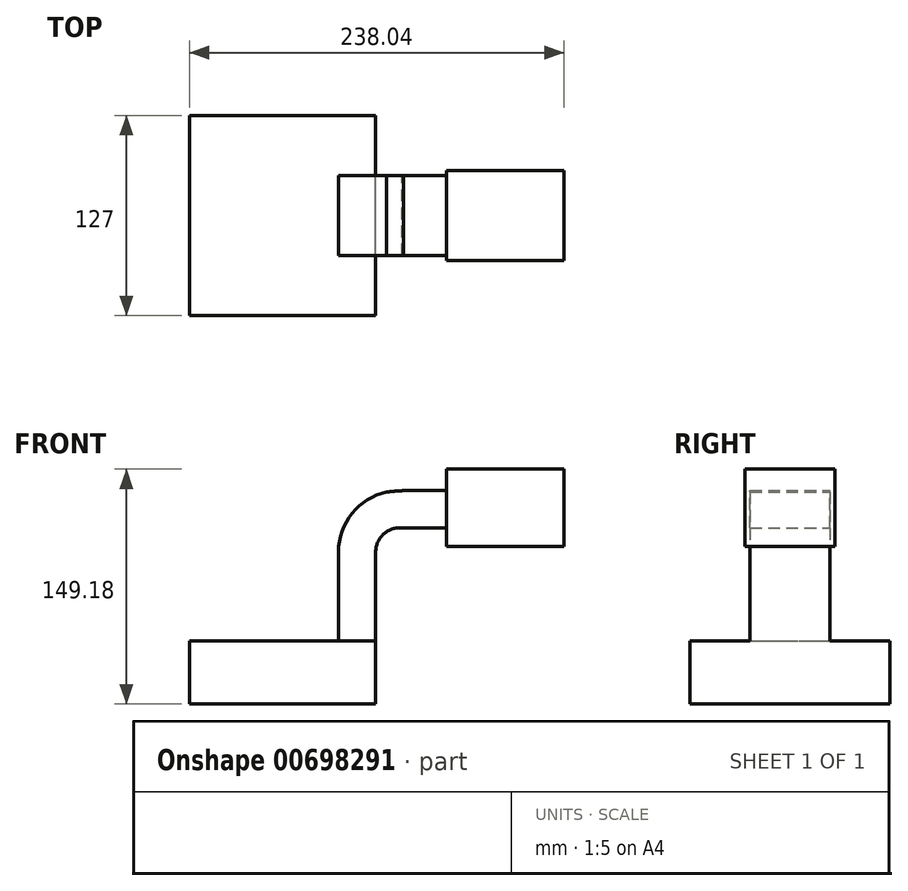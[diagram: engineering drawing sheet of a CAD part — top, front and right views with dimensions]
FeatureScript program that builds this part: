
annotation { "Feature Type Name" : "Feature", "Feature Type Description" : "" }
export const myFeature = defineFeature(function(context is Context, id is Id, definition is map)
    precondition{}
    {
        {
            var Q0;
            Q0=qCreatedBy(makeId("Front.planeOp"),FACE);
            var sketch = newSketch(context, id + "F0", { "sketchPlane" : qUnion([Q0])});
            skLineSegment(sketch, "E0.bottom", {"start": v(-59.16, 20.08) * mm, "end": v(59.16, 20.08) * mm});
            skLineSegment(sketch, "E0.top", {"start": v(-59.16, -20.08) * mm, "end": v(59.16, -20.08) * mm});
            skLineSegment(sketch, "E0.left", {"start": v(-59.16, 20.08) * mm, "end": v(-59.16, -20.08) * mm});
            skLineSegment(sketch, "E0.right", {"start": v(59.16, 20.08) * mm, "end": v(59.16, -20.08) * mm});
            skPoint(sketch, "E0.middle", {"position": v(0, 0) * mm});
            skLineSegment(sketch, "E1.bottom", {"start": v(104.17, 79.98) * mm, "end": v(178.88, 79.98) * mm});
            skLineSegment(sketch, "E1.top", {"start": v(104.17, 129.1) * mm, "end": v(178.88, 129.1) * mm});
            skLineSegment(sketch, "E1.left", {"start": v(104.17, 79.98) * mm, "end": v(104.17, 129.1) * mm});
            skLineSegment(sketch, "E1.right", {"start": v(178.88, 79.98) * mm, "end": v(178.88, 129.1) * mm});
            skPoint(sketch, "E1.middle", {"position": v(141.53, 104.54) * mm});
            skLineSegment(sketch, "E2", {"start": v(59.16, 20.08) * mm, "end": v(59.16, 76.4) * mm});
            skArc(sketch, "E3", {"start": v(59.16, 76.4) * mm, "mid": v(64.2, 87.8) * mm, "end": v(76.02, 91.75) * mm});
            skLineSegment(sketch, "E4", {"start": v(76.02, 91.75) * mm, "end": v(141.53, 91.75) * mm});
            skPoint(sketch, "E4.endSnap0", {"position": v(141.53, 79.98) * mm});
            skLineSegment(sketch, "E5.0", {"start": v(76.87, 115.39) * mm, "end": v(141.53, 115.39) * mm});
            skArc(sketch, "E5.1", {"start": v(35.53, 76.4) * mm, "mid": v(47.79, 104.81) * mm, "end": v(76.87, 115.39) * mm});
            skLineSegment(sketch, "E5.2", {"start": v(35.53, 20.08) * mm, "end": v(35.53, 76.4) * mm});
            skLineSegment(sketch, "E6", {"start": v(141.53, 129.1) * mm, "end": v(141.53, 79.98) * mm});
            skFitSpline(sketch, "E7", {"points": [v(-59.16, 20.08) * mm, v(76.87, 115.39) * mm], "startDerivative": vector(43.21, 182.75) * mm, "endDerivative": vector(182.19, 9.5) * mm});
            skSolve(sketch);
        }
        {
            var Q0;
            Q0=makeQuery(id+"F0.imprint","IMPRINT",FACE,{"disambiguationData":[TD([[makeQuery(id+"F0.imprint","IMPRINT",EDGE,{"derivedFrom":sQuery(id+"F0.wireOp",EDGE,"E0.top")}),1.0]])]});
            extrude(context, id + "F1", {"entities" : qUnion([Q0]), "endBound" : BoundingType.SYMMETRIC, "depth" : 127 * mm, "offsetDistance" : 25.4 * mm});
        }
        {
            var Q0;
            {var subQ1=sQuery(id+"F0.wireOp",EDGE,"E2");Q0=makeQuery(id+"F0.imprint","IMPRINT",FACE,{"disambiguationData":[TD([[makeQuery(id+"F0.imprint","IMPRINT",EDGE,{"derivedFrom":subQ1}),1.0]])]});}
            extrude(context, id + "F2", {"entities" : qUnion([Q0]), "operationType" : NewBodyOperationType.ADD, "endBound" : BoundingType.SYMMETRIC, "depth" : 50.8 * mm, "offsetDistance" : 25.4 * mm});
        }
        {
            var Q0;
            {var subQ0=sQuery(id+"F0.wireOp",EDGE,"E1.left");var subQ1=sQuery(id+"F0.wireOp",EDGE,"E1.top");var subQ2=makeQuery(id+"F0.imprint","INTERSECT",VERTEX,{"derivedFrom":[subQ1,subQ0]});Q0=makeQuery(id+"F0.imprint","IMPRINT",FACE,{"disambiguationData":[TD([[makeQuery(id+"F0.imprint","IMPRINT",EDGE,{"disambiguationData":[TD([[subQ2,-1.0]])],"derivedFrom":subQ1}),-1.0]])]});}
            var Q1;
            {var subQ0=sQuery(id+"F0.wireOp",EDGE,"E4");var subQ1=sQuery(id+"F0.wireOp",EDGE,"E1.left");var subQ2=makeQuery(id+"F0.imprint","INTERSECT",VERTEX,{"derivedFrom":[subQ1,subQ0]});Q1=makeQuery(id+"F0.imprint","IMPRINT",FACE,{"disambiguationData":[TD([[makeQuery(id+"F0.imprint","IMPRINT",EDGE,{"disambiguationData":[TD([[subQ2,-1.0]])],"derivedFrom":subQ1}),-1.0]])]});}
            var Q2;
            {var subQ0=sQuery(id+"F0.wireOp",EDGE,"E1.left");var subQ1=sQuery(id+"F0.wireOp",EDGE,"E1.bottom");var subQ2=makeQuery(id+"F0.imprint","INTERSECT",VERTEX,{"derivedFrom":[subQ1,subQ0]});Q2=makeQuery(id+"F0.imprint","IMPRINT",FACE,{"disambiguationData":[TD([[makeQuery(id+"F0.imprint","IMPRINT",EDGE,{"disambiguationData":[TD([[subQ2,-1.0]])],"derivedFrom":subQ1}),1.0]])]});}
            var Q3;
            {var subQ4=sQuery(id+"F0.wireOp",EDGE,"E1.right");Q3=makeQuery(id+"F0.imprint","IMPRINT",FACE,{"disambiguationData":[TD([[makeQuery(id+"F0.imprint","IMPRINT",EDGE,{"derivedFrom":subQ4}),1.0]])]});}
            extrude(context, id + "F3", {"entities" : qUnion([Q0, Q1, Q2, Q3]), "operationType" : NewBodyOperationType.ADD, "endBound" : BoundingType.SYMMETRIC, "depth" : 57.15 * mm, "offsetDistance" : 25.4 * mm});
        }
    });
